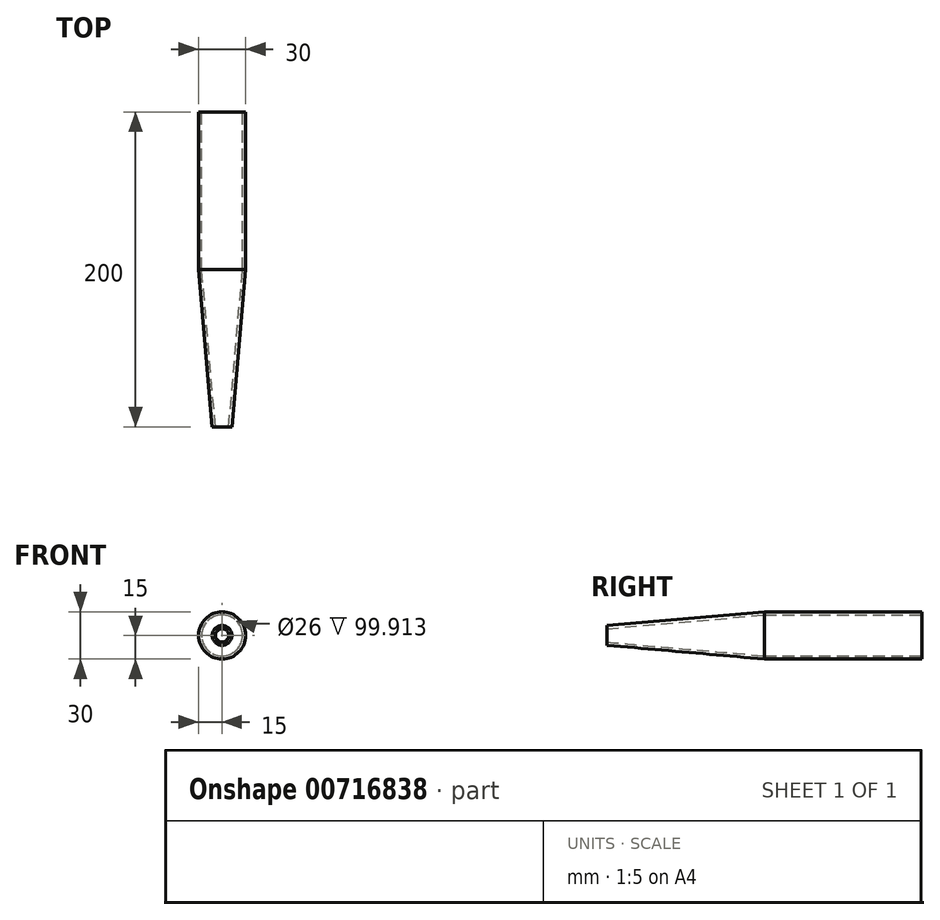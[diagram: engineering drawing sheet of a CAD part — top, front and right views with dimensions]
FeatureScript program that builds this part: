
annotation { "Feature Type Name" : "Feature", "Feature Type Description" : "" }
export const myFeature = defineFeature(function(context is Context, id is Id, definition is map)
    precondition{}
    {
        {
            var Q0;
            Q0=qCreatedBy(makeId("Front.planeOp"),FACE);
            var sketch = newSketch(context, id + "F0", { "sketchPlane" : qUnion([Q0])});
            skCircle(sketch, "E0", {"center": v(0, 0) * mm, "radius": 15 * mm});
            skSolve(sketch);
        }
        {
            var Q0;
            Q0 = qSketchRegion(id + "F0", true);
            extrude(context, id + "F1", {"entities" : qUnion([Q0]), "depth" : 100 * mm, "offsetDistance" : 25 * mm, "hasDraft" : true, "draftAngle" : 5 * degree, "draftPullDirection" : true, "hasSecondDirection" : true, "secondDirectionOppositeDirection" : true, "secondDirectionDepth" : 100 * mm});
        }
        {
            var Q0;
            Q0=makeQuery(id+"F1.opExtrude","CAP_FACE",FACE,{"disambiguationData":[OSD([sQuery(id+"F0.wireOp",EDGE,"E0")])],"isStart":true});
            var Q1;
            Q1=makeQuery(id+"F1.opExtrude","CAP_FACE",FACE,{"disambiguationData":[OSD([sQuery(id+"F0.wireOp",EDGE,"E0")])],"isStart":false});
            shell(context, id + "F2", {"entities" : qUnion([Q0, Q1]), "thickness" : 2 * mm});
        }
    });
